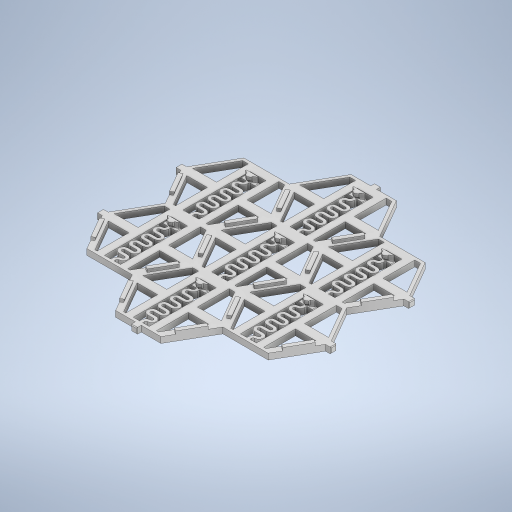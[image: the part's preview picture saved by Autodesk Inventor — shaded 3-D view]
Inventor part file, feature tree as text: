
AUTODESK INVENTOR PART (.ipt)
format: ipt  version: 2024 (Build 280153000, 153)  size: 1,873,408 bytes
history: native  units: in
note: dims shown in document units (in); Inventor stores cm internally (conversion verified against a paired STEP export)
features: move_body x29, direct_edit x19, extrude x12, sketch x6, chamfer x5, draft x2, plane x2, pattern_linear x1, pattern_circular x1, boolean_combine x1, other x1
ambient origin geometry x8: Origin, YZ Plane, XZ Plane, XY Plane, X Axis, Y Axis, Z Axis, Center Point
bodies: Solid1 (feature_tree), Solid8 (feature_tree)
feature tree (79):
  sketch  "Sketch1"  dims[d0=0.5217in d1=1.939in d2=120.0deg d3=120.0deg d4=0.4134in d5=0.9695in d6=0.0709in d7=0.0709in d8=0.1378in d9=0.8268in d10=0.1181in]
  extrude  "Extrusion1"  Depth=0.1181in
  extrude  "Extrusion2"  Depth=0.0787in
  extrude  "Extrusion3"  Depth=0.0787in
  chamfer  "Chamfer1"  Distance=1.5748in
  extrude  "Extrusion4"  Depth=0.0394in
  chamfer  "Chamfer2"  Distance=0.0787in
  direct_edit  "Direct Edit1"
  direct_edit  "Direct Edit2"
  direct_edit  "Direct Edit3"
  direct_edit  "Direct Edit4"
  direct_edit  "Direct Edit5"
  direct_edit  "Direct Edit6"
  direct_edit  "Direct Edit7"
  direct_edit  "Direct Edit8"
  direct_edit  "Direct Edit9"
  direct_edit  "Direct Edit10"
  extrude  "Extrusion7"  Depth=0.315in
  chamfer  "Chamfer3"  Distance=0.0157in
  direct_edit  "Direct Edit11"
  direct_edit  "Direct Edit12"
  extrude  "Extrusion8"  Depth=0.0787in
  extrude  "Extrusion9"  Depth=0.1181in
  draft  "FaceDraft1"
  draft  "FaceDraft2"
  direct_edit  "Direct Edit13"
  direct_edit  "Direct Edit14"
  direct_edit  "Direct Edit15"
  direct_edit  "Direct Edit16"
  direct_edit  "Direct Edit17"
  direct_edit  "Direct Edit18"
  direct_edit  "Direct Edit19"
  extrude  "Extrusion10"  Depth=0.1969in
  chamfer  "Chamfer4"  Distance=0.0787in
  pattern_linear  "Rectangular Pattern1"  Spacing1=0.1181in  [1 undecoded]
  pattern_circular  "Circular Pattern2"  [2 undecoded]
  boolean_combine  "Combine1"
  plane  "Work Plane1"
  extrude  "Extrusion11"  Depth=0.0787in
  plane  "Work Plane2"
  extrude  "Extrusion12"  Depth=0.0787in
  sketch  "Sketch7"  dims[d17=0.0394in d19=1.5748in d21=0.315in d22=0.3937in d24=0.3937in d26=0.0394in d27=0.0787in d28=0.315in d29=0.0157in d30=0.0157in d31=0.1181in d32=0.1969in d33=0.0787in d34=0.0in d35=0.1181in d36=0.0in d37=0.0787in d38=0.0079in d39=0.0787in d40=0.0079in d41=0.0787in d42=0.0079in d43=0.0079in d44=0.0787in d45=0.0394in d46=0.0197in d47=0.0394in d48=0.0in d49=0.0197in d50=0.0787in d51=45.0deg d52=0.0197in d53=0.0in d54=0.0079in d55=0.0787in d56=45.0deg d57=0.0in d58=0.0in d59=0.0098in d60=0.0in d61=0.0in d62=0.0098in d63=0.0in d64=0.0in d65=-0.0197in d66=0.0in d67=0.0in d68=-0.0197in d69=0.0in d70=0.0in d71=0.0153in d72=0.0in d73=0.0in d74=0.0153in d75=0.0in d76=0.0in d77=0.0153in d78=0.0in d79=0.0in d80=0.0153in d81=0.0in d82=0.0in d83=0.0394in d84=0.0in d85=0.0in d86=0.0394in d87=0.0in d88=0.0in d89=-0.0278in d90=0.0in d91=0.0in d92=-0.0278in d93=0.0in d94=0.0in d95=-0.0278in d96=0.0in d97=0.0in d98=-0.0278in d99=0.0in d100=-0.0157in d101=0.0in d102=0.0in d103=0.0157in d104=0.0in d116=0.0in d117=0.0in d118=0.0394in d119=0.1181in d120=0.0in d121=0.0276in d122=0.0787in d123=45.0deg d124=-0.0625in d125=0.0in d126=0.0in d127=0.0079in d128=0.0in d129=0.0in d130=0.315in d131=0.6299in d132=0.0787in d133=0.1575in d134=0.0in d135=0.1575in d136=0.0in d137=-0.1031in d138=-0.1031in d139=0.0591in d140=0.0in d141=0.0in d142=0.0in d143=-0.0197in d144=0.0in d145=0.0in d146=0.0197in d147=0.0in d148=0.0in d149=0.0in d150=0.0079in d151=0.0in d152=0.0in d153=0.0079in d154=0.0in d155=0.0in d156=0.0079in d157=0.0in d158=0.0in d159=0.0079in d163=0.0in d164=0.0in d165=-0.2992in d166=0.0in d167=0.0in d168=0.0039in d169=0.0in d170=0.0in d171=-0.0295in d172=1.378in d173=0.122in d174=0.122in d175=0.122in d176=0.122in d177=0.122in d178=0.0in d179=0.0197in d180=0.0787in d181=45.0deg d245=0.7874in d247=2.0965in d248=2.3622in d249=360.0deg d251=0.0787in d252=0.0787in d253=0.1969in d254=0.0in d255=-6.0525in d256=0.1969in d257=0.0in d258=0.0787in d259=0.0787in d260=0.1181in d261=0.0in d262=0.1181in d263=0.0in d264=0.0197in d265=0.0787in d266=45.0deg]
  extrude  "Extrusion13"  Depth=0.0787in
  extrude  "Extrusion14"  Depth=0.0787in
  chamfer  "Chamfer5"  Distance=0.0079in
  sketch  "Sketch3"  dims[d11=0.0394in d12=0.0787in]
  sketch  "Sketch4"  dims[d13=0.0394in d14=0.0787in]
  other  "Pattern of Solid1:7"
  sketch  "Sketch5"  dims[d15=0.0591in]
  sketch  "Sketch6"  dims[d16=0.0394in]
  move_body  "Move1"
  move_body  "Move2"
  move_body  "Move3"
  move_body  "Move4"
  move_body  "Move5"
  move_body  "Move6"
  move_body  "Move7"
  move_body  "Move8"
  move_body  "Move9"
  move_body  "Move10"
  move_body  "Move11"
  move_body  "Move12"
  move_body  "Move13"
  move_body  "Move14"
  move_body  "Move15"
  move_body  "Move16"
  move_body  "Move18"
  move_body  "Move19"
  move_body  "Move20"
  move_body  "Move21"
  move_body  "Move22"
  move_body  "Move23"
  move_body  "Move24"
  move_body  "Move25"
  move_body  "Move26"
  move_body  "Move27"
  move_body  "Move29"
  move_body  "Move30"
  move_body  "Move31"
note: 3 required parameter values undecoded (feature->parameter linkage not recoverable at this tier; creation-order binding heuristic only, values carry confidence <= 0.55)
